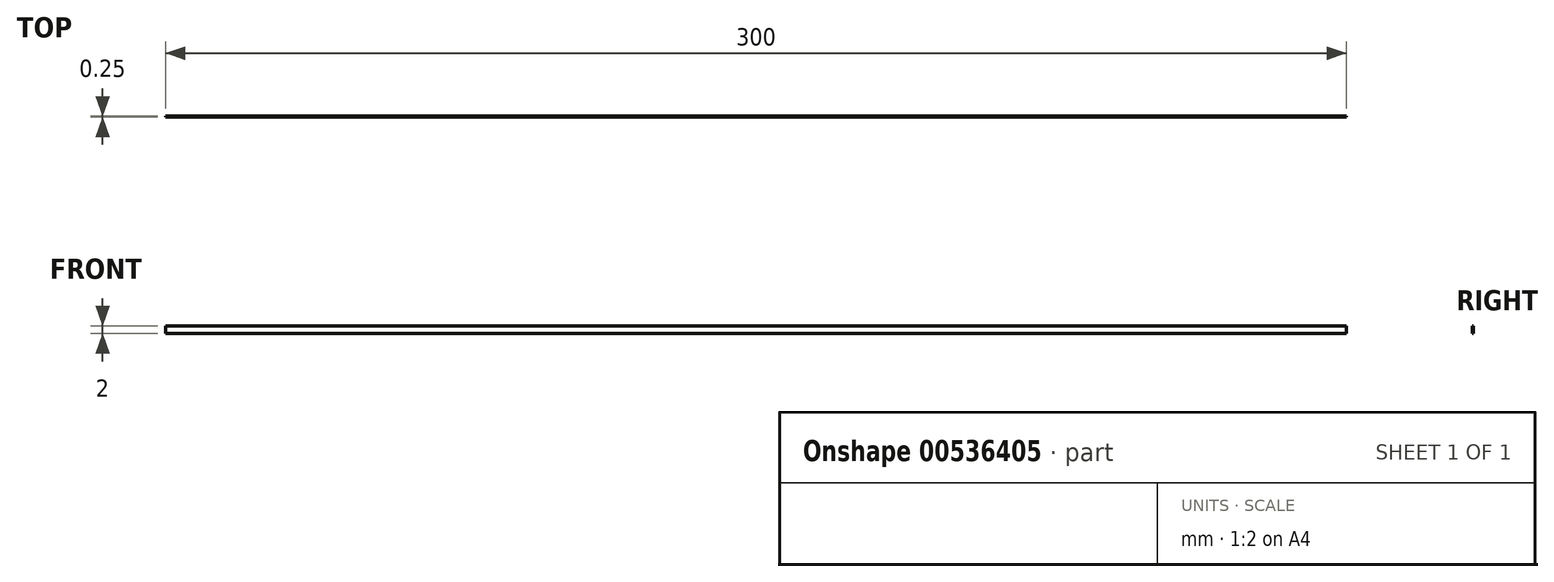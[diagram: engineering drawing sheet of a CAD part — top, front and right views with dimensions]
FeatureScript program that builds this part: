
annotation { "Feature Type Name" : "Feature", "Feature Type Description" : "" }
export const myFeature = defineFeature(function(context is Context, id is Id, definition is map)
    precondition{}
    {
        {
            var Q0;
            Q0=qCreatedBy(makeId("Front.planeOp"),FACE);
            var sketch = newSketch(context, id + "F0", { "sketchPlane" : qUnion([Q0])});
            skLineSegment(sketch, "E0.bottom", {"start": v(150, -1) * mm, "end": v(-150, -1) * mm});
            skLineSegment(sketch, "E0.top", {"start": v(150, 1) * mm, "end": v(-150, 1) * mm});
            skLineSegment(sketch, "E0.left", {"start": v(150, -1) * mm, "end": v(150, 1) * mm});
            skLineSegment(sketch, "E0.right", {"start": v(-150, -1) * mm, "end": v(-150, 1) * mm});
            skPoint(sketch, "E0.middle", {"position": v(0, 0) * mm});
            skSolve(sketch);
        }
        {
            var Q0;
            Q0=makeQuery(id+"F0.imprint","IMPRINT",FACE,{"disambiguationData":[TD([[makeQuery(id+"F0.imprint","IMPRINT",EDGE,{"derivedFrom":sQuery(id+"F0.wireOp",EDGE,"E0.bottom")}),-1.0]])]});
            extrude(context, id + "F1", {"entities" : qUnion([Q0]), "depth" : 0.25 * mm});
        }
    });
